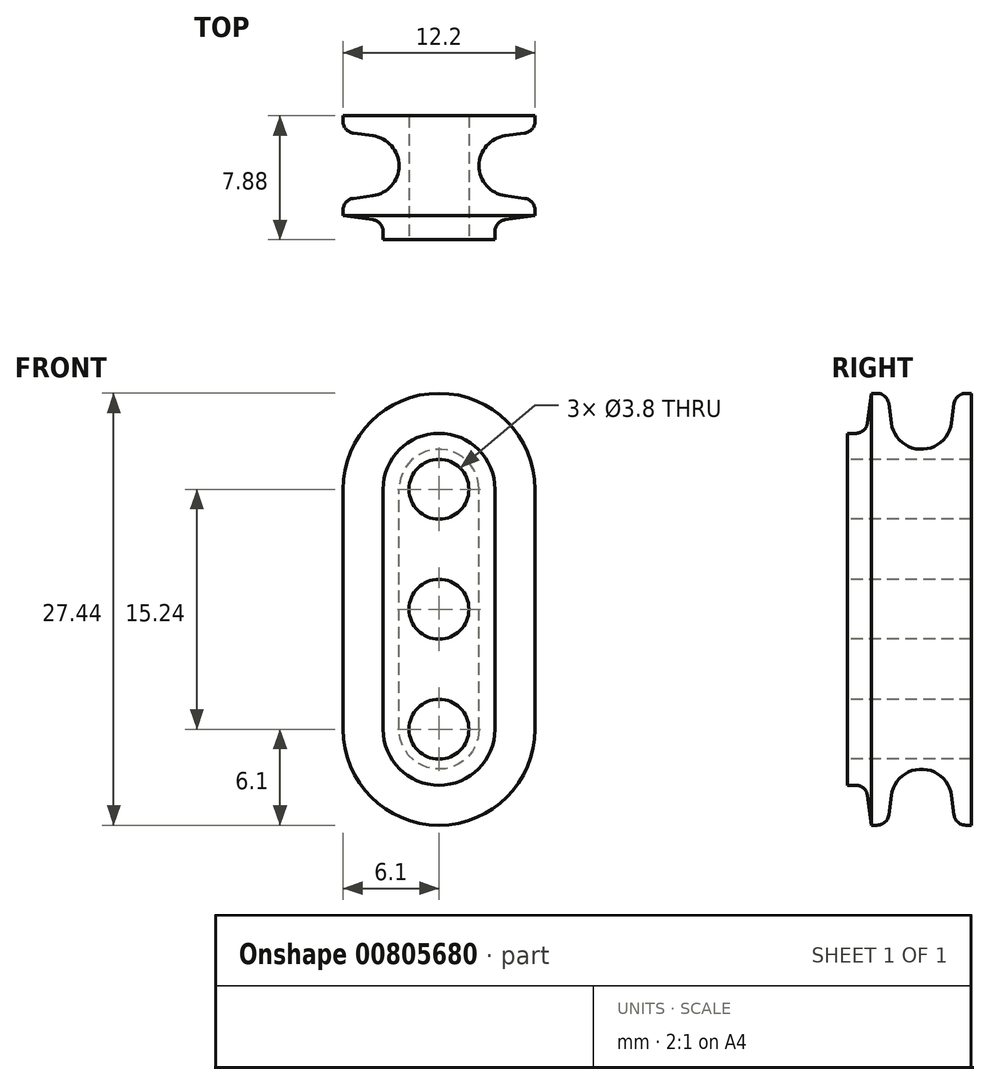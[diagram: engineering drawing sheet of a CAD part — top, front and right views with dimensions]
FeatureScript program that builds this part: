
annotation { "Feature Type Name" : "Feature", "Feature Type Description" : "" }
export const myFeature = defineFeature(function(context is Context, id is Id, definition is map)
    precondition{}
    {
        {
            var Q0;
            Q0=qCreatedBy(makeId("Front.planeOp"),FACE);
            var sketch = newSketch(context, id + "F0", { "sketchPlane" : qUnion([Q0])});
            skCircle(sketch, "E0", {"center": v(0, 0) * mm, "radius": 6.1 * mm});
            skSolve(sketch);
        }
        {
            var Q0;
            Q0=makeQuery(id+"F0.imprint","IMPRINT",FACE,{"disambiguationData":[TD([[makeQuery(id+"F0.imprint","IMPRINT",EDGE,{"derivedFrom":sQuery(id+"F0.wireOp",EDGE,"E0")}),1.0]])]});
            extrude(context, id + "F1", {"entities" : qUnion([Q0]), "depth" : 6.35 * mm, "offsetDistance" : 25.4 * mm, "symmetric" : true});
        }
        {
            var Q0;
            Q0=qCreatedBy(makeId("Front.planeOp"),FACE);
            var sketch = newSketch(context, id + "F2", { "sketchPlane" : qUnion([Q0])});
            skLineSegment(sketch, "E1.bottom", {"start": v(12.6, 0) * mm, "end": v(-13.53, 0) * mm});
            skLineSegment(sketch, "E1.top", {"start": v(12.6, -24.15) * mm, "end": v(-13.53, -24.15) * mm});
            skLineSegment(sketch, "E1.left", {"start": v(12.6, 0) * mm, "end": v(12.6, -24.15) * mm});
            skLineSegment(sketch, "E1.right", {"start": v(-13.53, 0) * mm, "end": v(-13.53, -24.15) * mm});
            skSolve(sketch);
        }
        {
            var Q0;
            Q0 = qSketchRegion(id + "F2", true);
            extrude(context, id + "F3", {"entities" : qUnion([Q0]), "operationType" : NewBodyOperationType.REMOVE, "oppositeDirection" : true, "depth" : 25.4 * mm, "offsetDistance" : 25.4 * mm, "symmetric" : true});
        }
        {
            var Q0;
            Q0=makeQuery(id+"F1.opExtrude","CAP_FACE",FACE,{"disambiguationData":[OSD([sQuery(id+"F0.wireOp",EDGE,"E0")])],"isStart":false});
            var sketch = newSketch(context, id + "F4", { "sketchPlane" : qUnion([Q0])});
            skCircle(sketch, "E2", {"center": v(0, 0) * mm, "radius": 1.9 * mm});
            skSolve(sketch);
        }
        {
            var Q0;
            {var subQ0=makeQuery(id+"F8.boolean.opBoolean","MERGE",FACE,{"derivedFrom":[makeQuery(id+"F1.opExtrude","CAP_FACE",FACE,{"disambiguationData":[OSD([sQuery(id+"F0.wireOp",EDGE,"E0")])],"isStart":false}),makeQuery(id+"F8.opExtrude","SWEPT_FACE",FACE,{"disambiguationData":[OSD([sQuery(id+"FHCKBcZkIibrD3C_1.wireOp",EDGE,"33893b92-1531-43ea-a95e-b28fcb7d8d0e.6")])]})]});Q0=makeQuery(id+"F9.boolean.opBoolean","MERGE",FACE,{"derivedFrom":[subQ0,makeQuery(id+"F9.opPattern","COPY",FACE,{"derivedFrom":subQ0,"instanceName":"1"})]});}
            extrude(context, id + "F5", {"entities" : qUnion([Q0]), "operationType" : NewBodyOperationType.ADD, "depth" : 1.52 * mm, "offsetDistance" : 25.4 * mm});
        }
        {
            var Q0;
            Q0=qCreatedBy(makeId("Right.planeOp"),FACE);
            var sketch = newSketch(context, id + "F6", { "sketchPlane" : qUnion([Q0])});
            skLineSegment(sketch, "E3", {"start": v(2.41, 7.99) * mm, "end": v(1.9, 4.2) * mm});
            skLineSegment(sketch, "E4", {"start": v(-2.41, 7.99) * mm, "end": v(-1.9, 4.2) * mm});
            skLineSegment(sketch, "E5", {"start": v(2.41, 7.99) * mm, "end": v(-2.41, 7.99) * mm});
            skArc(sketch, "E6", {"start": v(-1.9, 4.2) * mm, "mid": v(0, 2.54) * mm, "end": v(1.9, 4.2) * mm});
            skLineSegment(sketch, "E7", {"start": v(11.1, 0) * mm, "end": v(0, 0) * mm, "construction": true});
            skPoint(sketch, "E8", {"position": v(0, 2.54) * mm});
            skLineSegment(sketch, "E9", {"start": v(0, 0) * mm, "end": v(0, 4.46) * mm, "construction": true});
            skLineSegment(sketch, "E10.0", {"start": v(3.18, 0) * mm, "end": v(3.18, 6.1) * mm, "construction": true});
            skPoint(sketch, "E11", {"position": v(2.16, 6.1) * mm});
            skPoint(sketch, "E12", {"position": v(-2.16, 6.1) * mm});
            skLineSegment(sketch, "E13.1.0.0", {"start": v(-2.92, 7.99) * mm, "end": v(-3.43, 4.2) * mm});
            skLineSegment(sketch, "E13.direction1", {"start": v(-1.9, 4.2) * mm, "end": v(-7.24, 4.2) * mm, "construction": true});
            skPoint(sketch, "E14", {"position": v(-3.18, 6.1) * mm});
            skLineSegment(sketch, "E15", {"start": v(2.16, 6.1) * mm, "end": v(3.18, 6.1) * mm, "construction": true});
            skLineSegment(sketch, "E16", {"start": v(-3.18, 6.1) * mm, "end": v(-2.16, 6.1) * mm, "construction": true});
            skArc(sketch, "E17", {"start": v(-3.43, 4.2) * mm, "mid": v(-3.68, 3.74) * mm, "end": v(-4.17, 3.56) * mm});
            skLineSegment(sketch, "E18", {"start": v(-4.17, 3.56) * mm, "end": v(-5.95, 3.56) * mm});
            skLineSegment(sketch, "E19", {"start": v(-5.95, 3.56) * mm, "end": v(-5.95, 7.99) * mm});
            skLineSegment(sketch, "E20", {"start": v(-5.95, 7.99) * mm, "end": v(-2.92, 7.99) * mm});
            skSolve(sketch);
        }
        {
            var Q0;
            Q0=makeQuery(id+"F6.imprint","IMPRINT",FACE,{"disambiguationData":[TD([[makeQuery(id+"F6.imprint","IMPRINT",EDGE,{"derivedFrom":sQuery(id+"F6.wireOp",EDGE,"E3")}),-1.0]])]});
            var Q1;
            Q1=makeQuery(id+"F6.imprint","IMPRINT",FACE,{"disambiguationData":[TD([[makeQuery(id+"F6.imprint","IMPRINT",EDGE,{"derivedFrom":sQuery(id+"F6.wireOp",EDGE,"E13.1.0.0")}),-1.0]])]});
            var Q2;
            Q2=sQuery(id+"F6.wireOp",EDGE,"E7");
            var Q3;
            Q3=sQuery(id+"F6.wireOp",EDGE,"E7");
            revolve(context, id + "F7", {"operationType" : NewBodyOperationType.REMOVE, "surfaceOperationType" : NewSurfaceOperationType.NEW, "entities" : qUnion([Q0, Q1]), "surfaceEntities" : qUnion([Q2]), "axis" : qUnion([Q3]), "revolveType" : RevolveType.FULL, "oppositeDirection" : true});
        }
        {
            var Q0;
            {var subQ0=sQuery(id+"F2.wireOp",EDGE,"E1.bottom");Q0=makeQuery(id+"F5.boolean.opBoolean","MERGE",FACE,{"derivedFrom":[makeQuery(id+"F3.boolean.opBoolean","COPY",FACE,{"derivedFrom":makeQuery(id+"F3.opExtrude","SWEPT_FACE",FACE,{"disambiguationData":[OSD([subQ0])]})}),makeQuery(id+"F5.opExtrude","SWEPT_FACE",FACE,{"disambiguationData":[OSD([sQuery(id+"F0.wireOp",EDGE,"E0"),subQ0])]})]});}
            extrude(context, id + "F8", {"entities" : qUnion([Q0]), "operationType" : NewBodyOperationType.ADD, "depth" : 7.62 * mm, "offsetDistance" : 25.4 * mm});
        }
        {
            var Q0;
            Q0=makeQuery(id+"F1.opExtrude","SWEPT_BODY",BODY,{"disambiguationData":[OSD([sQuery(id+"F0.wireOp",EDGE,"E0")])]});
            var Q1;
            Q1=makeQuery(id+"F8.opExtrude","CAP_FACE",FACE,{"disambiguationData":[OSD([sQuery(id+"F0.wireOp",EDGE,"E0"),sQuery(id+"F2.wireOp",EDGE,"E1.bottom")])],"isStart":false});
            mirror(context, id + "F9", {"operationType" : NewBodyOperationType.ADD, "entities" : qUnion([Q0]), "mirrorPlane" : qUnion([Q1])});
        }
        {
            var Q0;
            Q0=qSketchRegion(id+"F4",true);
            extrude(context, id + "F10", {"entities" : qUnion([Q0]), "operationType" : NewBodyOperationType.REMOVE, "oppositeDirection" : true, "depth" : 127 * mm, "offsetDistance" : 25.4 * mm, "symmetric" : true});
        }
        {
            var Q0;
            {var subQ0=sQuery(id+"F2.wireOp",EDGE,"E1.bottom");var subQ1=sQuery(id+"F0.wireOp",EDGE,"E0");var subQ2=makeQuery(id+"F8.boolean.opBoolean","MERGE",FACE,{"derivedFrom":[makeQuery(id+"F5.opExtrude","CAP_FACE",FACE,{"disambiguationData":[OSD([subQ1])],"isStart":false}),makeQuery(id+"F8.opExtrude","SWEPT_FACE",FACE,{"disambiguationData":[OSD([subQ1,subQ0]),TDD([makeQuery(id+"F5.opExtrude","CAP_EDGE",EDGE,{"disambiguationData":[OSD([subQ1,subQ0])],"isStart":false})])]})]});Q0=makeQuery(id+"F9.boolean.opBoolean","MERGE",FACE,{"derivedFrom":[subQ2,makeQuery(id+"F9.opPattern","COPY",FACE,{"derivedFrom":subQ2,"instanceName":"1"})]});}
            var sketch = newSketch(context, id + "F11", { "sketchPlane" : qUnion([Q0])});
            skCircle(sketch, "E21.0", {"center": v(0, 0) * mm, "radius": 1.9 * mm});
            skCircle(sketch, "E22.0.1.0", {"center": v(0, -7.62) * mm, "radius": 1.9 * mm});
            skCircle(sketch, "E22.0.2.0", {"center": v(0, -15.24) * mm, "radius": 1.9 * mm});
            skLineSegment(sketch, "E22.direction1", {"start": v(0, 0) * mm, "end": v(25.4, 0) * mm, "construction": true});
            skLineSegment(sketch, "E22.direction2", {"start": v(0, 0) * mm, "end": v(0, -7.62) * mm, "construction": true});
            skSolve(sketch);
        }
        {
            var Q0;
            Q0=makeQuery(id+"F11.imprint","IMPRINT",FACE,{"disambiguationData":[TD([[makeQuery(id+"F11.imprint","IMPRINT",EDGE,{"derivedFrom":sQuery(id+"F11.wireOp",EDGE,"E22.0.1.0")}),1.0]])]});
            var Q1;
            Q1=makeQuery(id+"F11.imprint","IMPRINT",FACE,{"disambiguationData":[TD([[makeQuery(id+"F11.imprint","IMPRINT",EDGE,{"derivedFrom":sQuery(id+"F11.wireOp",EDGE,"E22.0.2.0")}),1.0]])]});
            extrude(context, id + "F12", {"entities" : qUnion([Q0, Q1]), "operationType" : NewBodyOperationType.REMOVE, "endBound" : BoundingType.THROUGH_ALL, "oppositeDirection" : true, "depth" : 25.4 * mm, "offsetDistance" : 25.4 * mm});
        }
        {
            var Q0;
            {var subQ0=sQuery(id+"F0.wireOp",EDGE,"E0");Q0=makeQuery(id+"F7.boolean.opBoolean","INTERSECT",EDGE,{"derivedFrom":[makeQuery(id+"F5.boolean.opBoolean","MERGE",FACE,{"derivedFrom":[makeQuery(id+"F1.opExtrude","SWEPT_FACE",FACE,{"disambiguationData":[OSD([subQ0])]}),makeQuery(id+"F5.opExtrude","SWEPT_FACE",FACE,{"disambiguationData":[OSD([subQ0])]})]}),makeQuery(id+"F7.opRevolve","SWEPT_FACE",FACE,{"disambiguationData":[OSD([sQuery(id+"F6.wireOp",EDGE,"E4")])]})]});}
            var Q1;
            {var subQ0=sQuery(id+"F0.wireOp",EDGE,"E0");Q1=makeQuery(id+"F7.boolean.opBoolean","INTERSECT",EDGE,{"derivedFrom":[makeQuery(id+"F5.boolean.opBoolean","MERGE",FACE,{"derivedFrom":[makeQuery(id+"F1.opExtrude","SWEPT_FACE",FACE,{"disambiguationData":[OSD([subQ0])]}),makeQuery(id+"F5.opExtrude","SWEPT_FACE",FACE,{"disambiguationData":[OSD([subQ0])]})]}),makeQuery(id+"F7.opRevolve","SWEPT_FACE",FACE,{"disambiguationData":[OSD([sQuery(id+"F6.wireOp",EDGE,"E3")])]})]});}
            fillet(context, id + "F13", {"entities" : qUnion([Q0, Q1]), "radius" : 0.76 * mm, "tangentPropagation" : true, "allowEdgeOverflow" : false});
        }
    });
